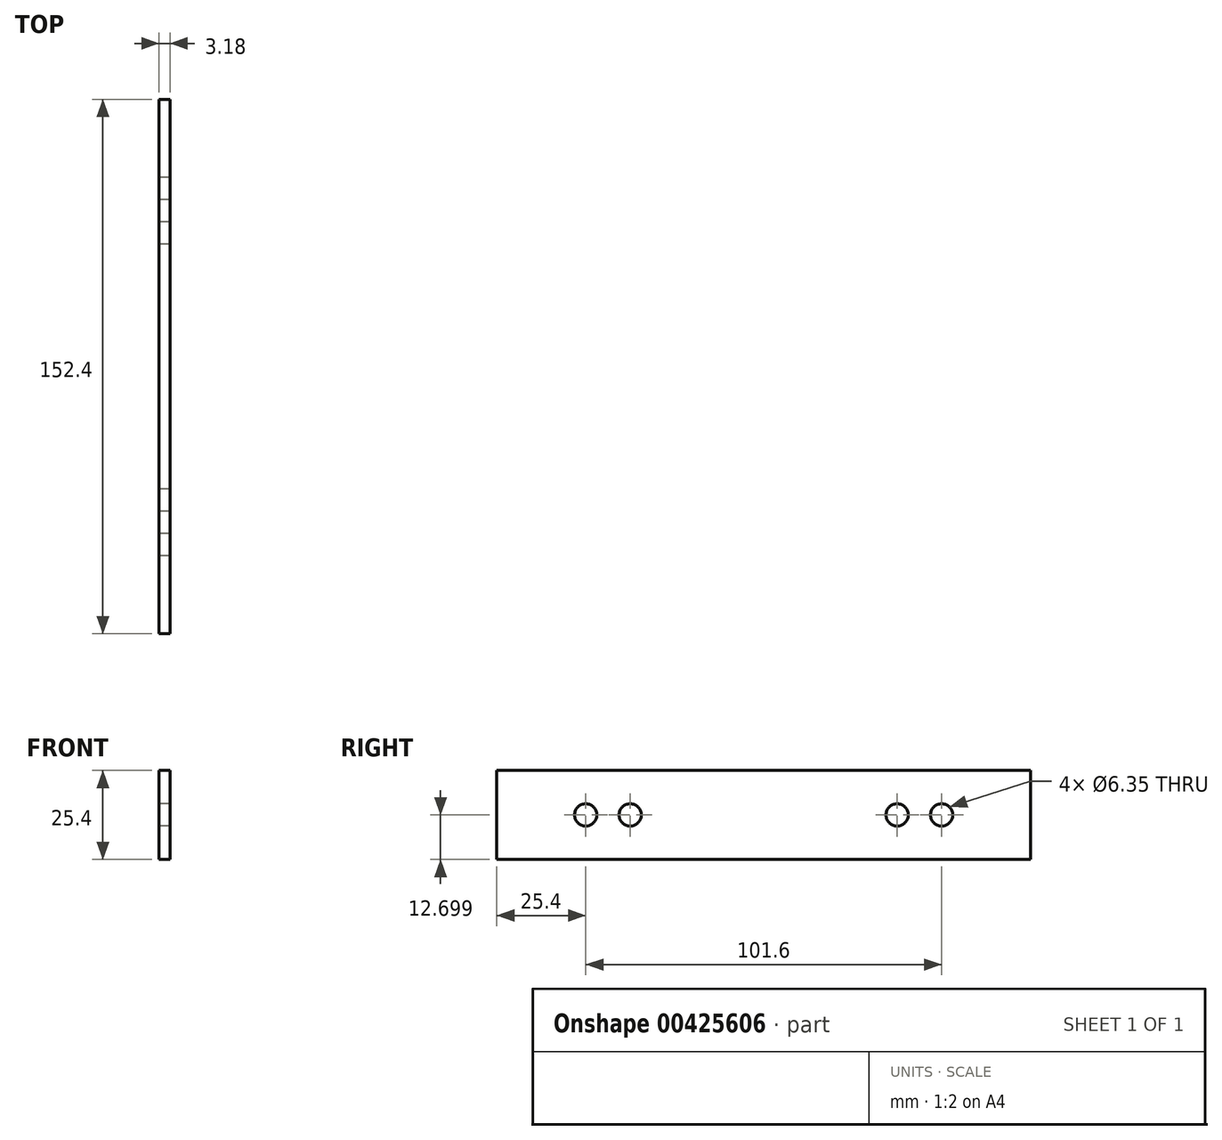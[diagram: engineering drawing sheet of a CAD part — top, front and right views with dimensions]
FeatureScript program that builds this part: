
annotation { "Feature Type Name" : "Feature", "Feature Type Description" : "" }
export const myFeature = defineFeature(function(context is Context, id is Id, definition is map)
    precondition{}
    {
        {
            var Q0;
            Q0=qCreatedBy(makeId("Right.planeOp"),FACE);
            var sketch = newSketch(context, id + "F0", { "sketchPlane" : qUnion([Q0])});
            skLineSegment(sketch, "E0.bottom", {"start": v(-73.04, 2.15) * mm, "end": v(79.36, 2.15) * mm});
            skLineSegment(sketch, "E0.top", {"start": v(-73.04, -23.25) * mm, "end": v(79.36, -23.25) * mm});
            skLineSegment(sketch, "E0.left", {"start": v(-73.04, 2.15) * mm, "end": v(-73.04, -23.25) * mm});
            skLineSegment(sketch, "E0.right", {"start": v(79.36, 2.15) * mm, "end": v(79.36, -23.25) * mm});
            skCircle(sketch, "E1", {"center": v(-47.64, -10.55) * mm, "radius": 3.18 * mm});
            skCircle(sketch, "E2", {"center": v(-34.94, -10.55) * mm, "radius": 3.18 * mm});
            skCircle(sketch, "E3", {"center": v(41.26, -10.55) * mm, "radius": 3.18 * mm});
            skCircle(sketch, "E4", {"center": v(53.96, -10.55) * mm, "radius": 3.18 * mm});
            skSolve(sketch);
        }
        {
            var Q0;
            Q0=makeQuery(id+"F0.imprint","IMPRINT",FACE,{"disambiguationData":[TD([[makeQuery(id+"F0.imprint","IMPRINT",EDGE,{"derivedFrom":sQuery(id+"F0.wireOp",EDGE,"E0.bottom")}),-1.0]])]});
            extrude(context, id + "F1", {"entities" : qUnion([Q0]), "depth" : 3.17 * mm});
        }
    });
